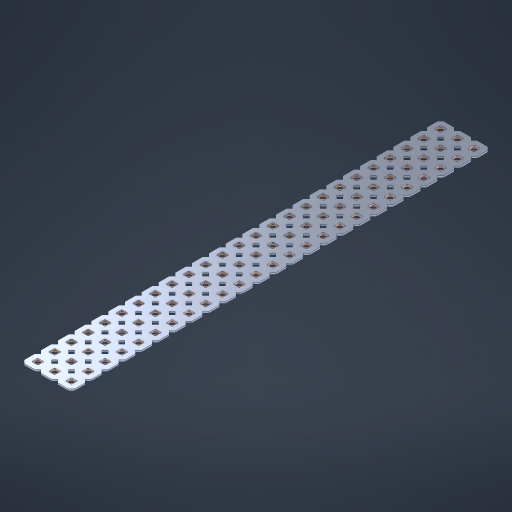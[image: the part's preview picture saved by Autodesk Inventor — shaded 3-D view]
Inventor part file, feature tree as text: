
AUTODESK INVENTOR PART (.ipt)
format: ipt  version: 2023 (Build 270158000, 158)  size: 1,133,056 bytes
history: native  units: in
note: dims shown in document units (in); Inventor stores cm internally (conversion verified against a paired STEP export)
features: other x76, extrude x74, sketch x2, pattern_linear x1
ambient origin geometry x8: Origin, YZ Plane, XZ Plane, XY Plane, X Axis, Y Axis, Z Axis, Center Point
bodies: Solid1 (feature_tree), Body (feature_tree)
feature tree (153):
  pattern_linear  "Rectangular Pattern1"  Spacing1=0.09in  [1 undecoded]
  sketch  "Sketch1"  dims[d1=0.5in]
  sketch  "Sketch2"  dims[d2=0.182in d3=0.09in d4=0.09in d5=0.09in d6=0.09in d7=0.09in d8=0.09in d9=0.09in d10=0.09in d11=0.02in d13=0.0in d14=0.172in d15=0.0625in d16=0.0in d19=0.5in d22=0.5in]
  other  "Srf1"
  other  "Srf126"
  other  "Srf127"
  other  "Srf128"
  other  "Srf129"
  other  "Srf130"
  other  "Srf131"
  other  "Srf250"
  other  "Srf251"
  other  "Srf252"
  other  "Srf253"
  other  "Srf254"
  other  "Srf255"
  other  "Srf256"
  other  "Srf257"
  other  "Srf258"
  other  "Srf259"
  other  "Srf260"
  other  "Srf261"
  other  "Srf262"
  other  "Srf263"
  other  "Srf264"
  other  "Srf265"
  other  "Srf266"
  other  "Srf267"
  other  "Srf268"
  other  "Srf269"
  other  "Srf270"
  other  "Srf271"
  other  "Srf272"
  other  "Srf273"
  other  "Srf274"
  other  "Srf275"
  other  "Srf276"
  other  "Srf277"
  other  "Srf278"
  other  "Srf279"
  other  "Srf280"
  other  "Srf281"
  other  "Srf282"
  other  "Srf283"
  other  "Srf284"
  other  "Srf285"
  other  "Srf286"
  other  "Srf287"
  other  "Srf288"
  other  "Srf289"
  other  "Srf290"
  other  "Srf291"
  other  "Srf292"
  other  "Srf293"
  other  "Srf294"
  other  "Srf295"
  other  "Srf296"
  other  "Srf297"
  other  "Srf298"
  other  "Srf299"
  other  "Srf300"
  other  "Srf301"
  other  "Srf302"
  other  "Srf303"
  other  "Srf304"
  other  "Srf305"
  other  "Srf306"
  other  "Srf307"
  other  "Srf308"
  other  "Srf309"
  other  "Srf310"
  other  "Srf311"
  other  "Srf312"
  other  "Srf313"
  other  "Srf314"
  other  "Srf315"
  other  "Srf316"
  other  "Srf317"
  other  "Circle"
  extrude  "ExtrusionSrf126"  Depth=0.09in
  extrude  "ExtrusionSrf127"  Depth=0.09in
  extrude  "ExtrusionSrf128"  Depth=0.09in
  extrude  "ExtrusionSrf129"  Depth=0.09in
  extrude  "ExtrusionSrf130"  Depth=0.09in
  extrude  "ExtrusionSrf131"  Depth=0.09in
  extrude  "ExtrusionSrf250"  Depth=0.09in
  extrude  "ExtrusionSrf251"  Depth=0.02in
  extrude  "ExtrusionSrf252"  TaperAngle=0.0deg  [1 undecoded]
  extrude  "ExtrusionSrf253"  Depth=0.5in
  extrude  "ExtrusionSrf254"  Depth=0.5in TaperAngle=0.0deg
  extrude  "ExtrusionSrf255"  Depth=0.5in
  extrude  "ExtrusionSrf256"  Depth=0.5in
  extrude  "ExtrusionSrf257"  [1 undecoded]
  extrude  "ExtrusionSrf258"  [1 undecoded]
  extrude  "ExtrusionSrf259"  [1 undecoded]
  extrude  "ExtrusionSrf260"  [1 undecoded]
  extrude  "ExtrusionSrf261"  [1 undecoded]
  extrude  "ExtrusionSrf262"  [1 undecoded]
  extrude  "ExtrusionSrf263"  [1 undecoded]
  extrude  "ExtrusionSrf264"  [1 undecoded]
  extrude  "ExtrusionSrf265"  [1 undecoded]
  extrude  "ExtrusionSrf266"  [1 undecoded]
  extrude  "ExtrusionSrf267"  [1 undecoded]
  extrude  "ExtrusionSrf268"  [1 undecoded]
  extrude  "ExtrusionSrf269"  [1 undecoded]
  extrude  "ExtrusionSrf270"  [1 undecoded]
  extrude  "ExtrusionSrf271"  [1 undecoded]
  extrude  "ExtrusionSrf272"  [1 undecoded]
  extrude  "ExtrusionSrf273"  [1 undecoded]
  extrude  "ExtrusionSrf274"  [1 undecoded]
  extrude  "ExtrusionSrf275"  [1 undecoded]
  extrude  "ExtrusionSrf276"  [1 undecoded]
  extrude  "ExtrusionSrf277"  [1 undecoded]
  extrude  "ExtrusionSrf278"  [1 undecoded]
  extrude  "ExtrusionSrf279"  [1 undecoded]
  extrude  "ExtrusionSrf280"  [1 undecoded]
  extrude  "ExtrusionSrf281"  [1 undecoded]
  extrude  "ExtrusionSrf282"  [1 undecoded]
  extrude  "ExtrusionSrf283"  [1 undecoded]
  extrude  "ExtrusionSrf284"  [1 undecoded]
  extrude  "ExtrusionSrf285"  [1 undecoded]
  extrude  "ExtrusionSrf286"  [1 undecoded]
  extrude  "ExtrusionSrf287"  [1 undecoded]
  extrude  "ExtrusionSrf288"  [1 undecoded]
  extrude  "ExtrusionSrf289"  [1 undecoded]
  extrude  "ExtrusionSrf290"  [1 undecoded]
  extrude  "ExtrusionSrf291"  [1 undecoded]
  extrude  "ExtrusionSrf292"  [1 undecoded]
  extrude  "ExtrusionSrf293"  [1 undecoded]
  extrude  "ExtrusionSrf294"  [1 undecoded]
  extrude  "ExtrusionSrf295"  [1 undecoded]
  extrude  "ExtrusionSrf296"  [1 undecoded]
  extrude  "ExtrusionSrf297"  [1 undecoded]
  extrude  "ExtrusionSrf298"  [1 undecoded]
  extrude  "ExtrusionSrf299"  [1 undecoded]
  extrude  "ExtrusionSrf300"  [1 undecoded]
  extrude  "ExtrusionSrf301"  [1 undecoded]
  extrude  "ExtrusionSrf302"  [1 undecoded]
  extrude  "ExtrusionSrf303"  [1 undecoded]
  extrude  "ExtrusionSrf304"  [1 undecoded]
  extrude  "ExtrusionSrf305"  [1 undecoded]
  extrude  "ExtrusionSrf306"  [1 undecoded]
  extrude  "ExtrusionSrf307"  [1 undecoded]
  extrude  "ExtrusionSrf308"  [1 undecoded]
  extrude  "ExtrusionSrf309"  [1 undecoded]
  extrude  "ExtrusionSrf310"  [1 undecoded]
  extrude  "ExtrusionSrf311"  [1 undecoded]
  extrude  "ExtrusionSrf312"  [1 undecoded]
  extrude  "ExtrusionSrf313"  [1 undecoded]
  extrude  "ExtrusionSrf314"  [1 undecoded]
  extrude  "ExtrusionSrf315"  [1 undecoded]
  extrude  "ExtrusionSrf316"  [1 undecoded]
  extrude  "ExtrusionSrf317"  [1 undecoded]
note: 63 required parameter values undecoded (feature->parameter linkage not recoverable at this tier; creation-order binding heuristic only, values carry confidence <= 0.55)
